# Revit family: Sanitary_Shower-screens_Duscholux_DuschoGredel_DuschoAnker_Slider-door-bath
name_source: partatom
category: Plumbing Fixtures
revit_build: Autodesk Revit 2017 (Build: 20160225_1515(x64)
units: mm (PartAtom-declared; Revit-internal decimal feet)

## family parameters
Always vertical = Yes
Cut with Voids When Loaded = No
OmniClass Number = 23.45.00.00
OmniClass Title = Sanitary, Laundry, and Cleaning Equipment
Part Type = Normal
Room Calculation Point = No
Round Connector Dimension = Use Diameter
Shared = No
Work Plane-Based = No

## types (4) — shared parameters
Assembly Code = C1030200
Certified Quality UNE EN 14428 = http://www.duscholux.es
Combinations = Lateral 90°
Configuration enclosure = http://configuratumampara.duscholux.es
Description = Front 1 fixed + 1 sliding door for bath
Design country = Spain / Germany
Edition number = 1
Environmental Management ISO 14001 = ECOEMBES Certificate
Fact Sheet = http://blob.duscholux.es
Glass Material = Glass_Material-Duscholux
Glass in Building UNE EN 12150 = CE Conformity marking
Height = 1600 mm  [stored 5.24934 ft]
IFC Classification = Furnishing Element
Image = http://www.duscholux.es
Logo visibility = Yes
Maintenance and Cleaning = http://www.duscholux.es
Manufacturer = Duscholux Ibérica, S.A.
Manufacturer country = Spain
Manufacturer name = Duscholux Ibérica, S.A.
Max Height = 1600 mm  [stored 5.24934 ft]
Min Max Width = 1500 mm  [stored 4.92126 ft]
Model = DuschoAnker
NBS Reference Code = 45-35-70
NBS Reference Description = Shower Enclosures
Net Weight (Kg) = 42.3
Opening System = Sliding
Opening System Image = http://blob.duscholux.es
Optional = Towel rail / Shelf
Product family = Duscho Gredel
Products = http://www.duscholux.es
Ref. = 6PI / 6PD
Series = Duscho Gredel
Sliding Door Width = 719 mm  [stored 2.35892 ft]
Technical Inspection Certificate (Applus) = http://www.duscholux.es
Text logo visibility = Yes
Thickness Safety Glass Fixed Panel = 8 mm  [stored 0.0262467 ft]
Thickness Safety Glass Sliding = 5 mm  [stored 0.0164042 ft]
UNSPSC Code = 30181507
URL = http://www.duscholux.es
Uniclass 2015 Code = PR-40-20-06-79
Uniclass 2015 Description = Shower Enclosures
Width = 1500 mm  [stored 4.92126 ft]
zero-valued in all types: Opening Door, Opening Percentage

## per-type parameters (varying)
| type | Accesories Material | Bath Height | Brand | Components | Handle Height | Handle Material | Product group |
| White Aluminium Finish | White Finish Acc | 400 mm  [stored 1.31234 ft] | Duschoux | Eropean components | 1200 mm | White Finish Acc | front for bath |
| Silver Matt Aluminium Finish | Chrome Finish | 400 mm  [stored 1.31234 ft] | Duscholux | Eropean components | 1200 mm | Zamak | Front for bath |
| Platinum Aluminium Finish | Silver Matt Finish | 450 mm  [stored 1.47638 ft] | Duscholux | European components | 1250 mm  [stored 4.10105 ft] | Zamak | front for bath |
| Black Aluminium Finish | Chrome Finish | 400 mm  [stored 1.31234 ft] | Duscholux | European components | 1200 mm | Zamak | Fornt for bath |

note: column(s) folded — value = type name in every type: Frame Material

note: [stored X ft] marks values corroborated as IEEE doubles in the binary element streams (Revit-internal decimal feet)

## geometry (parser evidence)
native form markers: Sweep x3
no freeform markers — native parametric forms only
